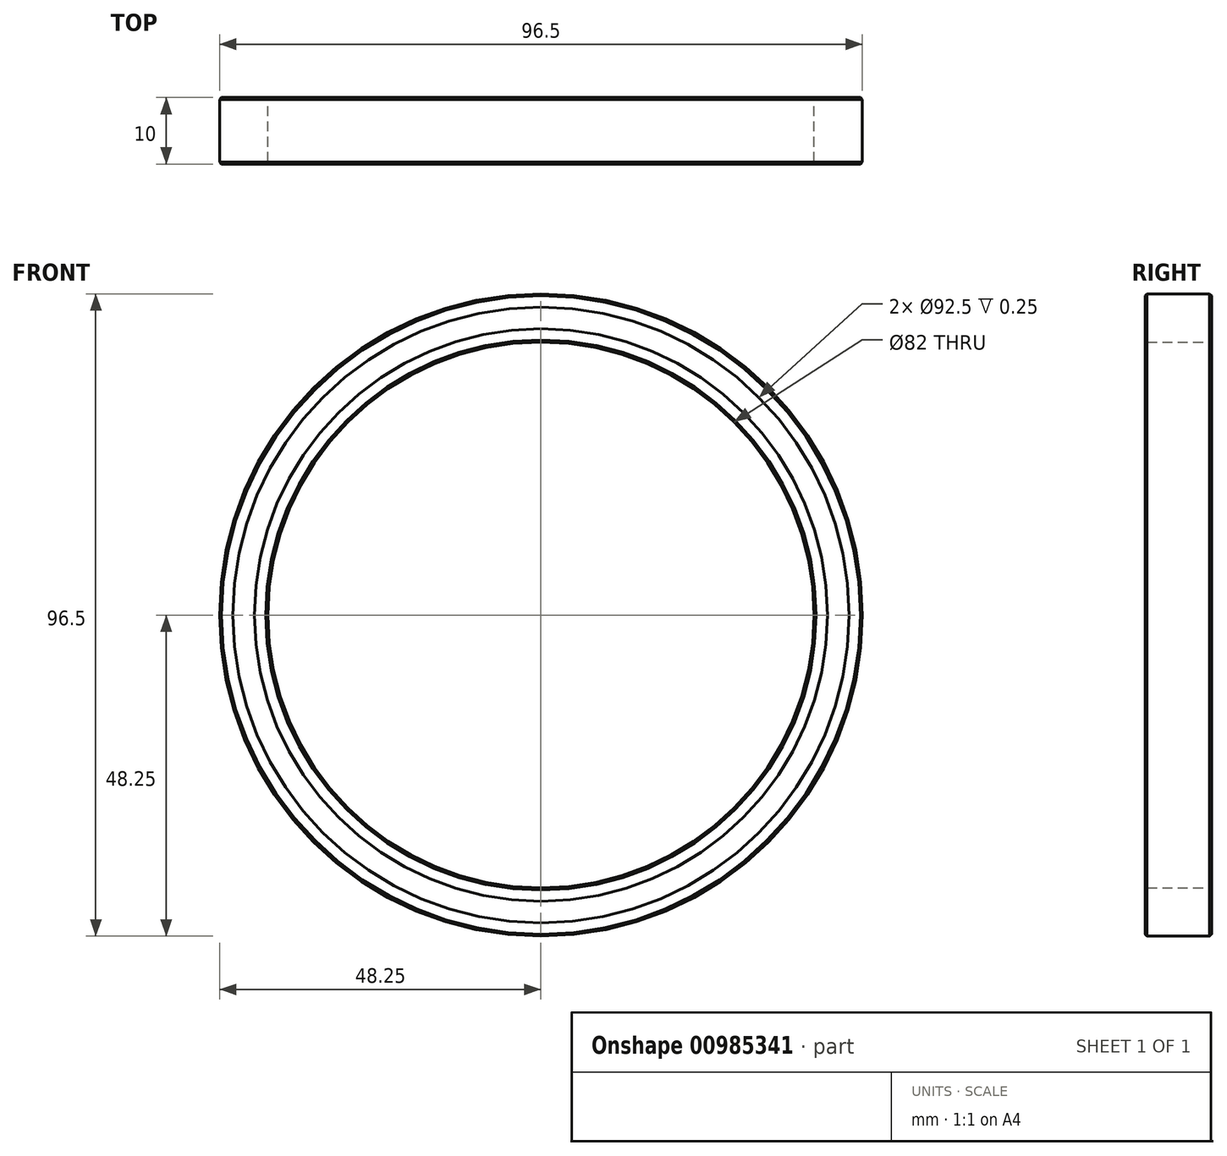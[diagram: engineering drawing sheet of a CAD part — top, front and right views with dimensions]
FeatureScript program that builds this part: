
annotation { "Feature Type Name" : "Feature", "Feature Type Description" : "" }
export const myFeature = defineFeature(function(context is Context, id is Id, definition is map)
    precondition{}
    {
        {
            var Q0;
            Q0=qCreatedBy(makeId("Front.planeOp"),FACE);
            var sketch = newSketch(context, id + "F0", { "sketchPlane" : qUnion([Q0])});
            skCircle(sketch, "E0", {"center": v(0, 0) * mm, "radius": 41 * mm});
            skCircle(sketch, "E1", {"center": v(0, 0) * mm, "radius": 43 * mm});
            skCircle(sketch, "E2", {"center": v(0, 0) * mm, "radius": 46.25 * mm});
            skCircle(sketch, "E3", {"center": v(0, 0) * mm, "radius": 48.25 * mm});
            skSolve(sketch);
        }
        {
            var Q0;
            Q0=makeQuery(id+"F0.imprint","IMPRINT",FACE,{"disambiguationData":[TD([[makeQuery(id+"F0.imprint","IMPRINT",EDGE,{"derivedFrom":sQuery(id+"F0.wireOp",EDGE,"E2")}),-1.0]])]});
            var Q1;
            Q1=makeQuery(id+"F0.imprint","IMPRINT",FACE,{"disambiguationData":[TD([[makeQuery(id+"F0.imprint","IMPRINT",EDGE,{"derivedFrom":sQuery(id+"F0.wireOp",EDGE,"E0")}),-1.0]])]});
            extrude(context, id + "F1", {"entities" : qUnion([Q0, Q1]), "endBound" : BoundingType.SYMMETRIC, "depth" : 10 * mm});
        }
        {
            var Q0;
            Q0=makeQuery(id+"F0.imprint","IMPRINT",FACE,{"disambiguationData":[TD([[makeQuery(id+"F0.imprint","IMPRINT",EDGE,{"derivedFrom":sQuery(id+"F0.wireOp",EDGE,"E1")}),-1.0]])]});
            extrude(context, id + "F2", {"entities" : qUnion([Q0]), "operationType" : NewBodyOperationType.ADD, "endBound" : BoundingType.SYMMETRIC, "depth" : 9.5 * mm});
        }
        {
            var Q0;
            Q0=makeQuery(id+"F1.opExtrude","SWEPT_FACE",FACE,{"disambiguationData":[OSD([sQuery(id+"F0.wireOp",EDGE,"E3")])]});
            var Q1;
            Q1=makeQuery(id+"F1.opExtrude","SWEPT_FACE",FACE,{"disambiguationData":[OSD([sQuery(id+"F0.wireOp",EDGE,"E0")])]});
            chamfer(context, id + "F3", {"entities" : qUnion([Q0, Q1]), "width" : 0.3 * mm, "tangentPropagation" : true});
        }
    });
